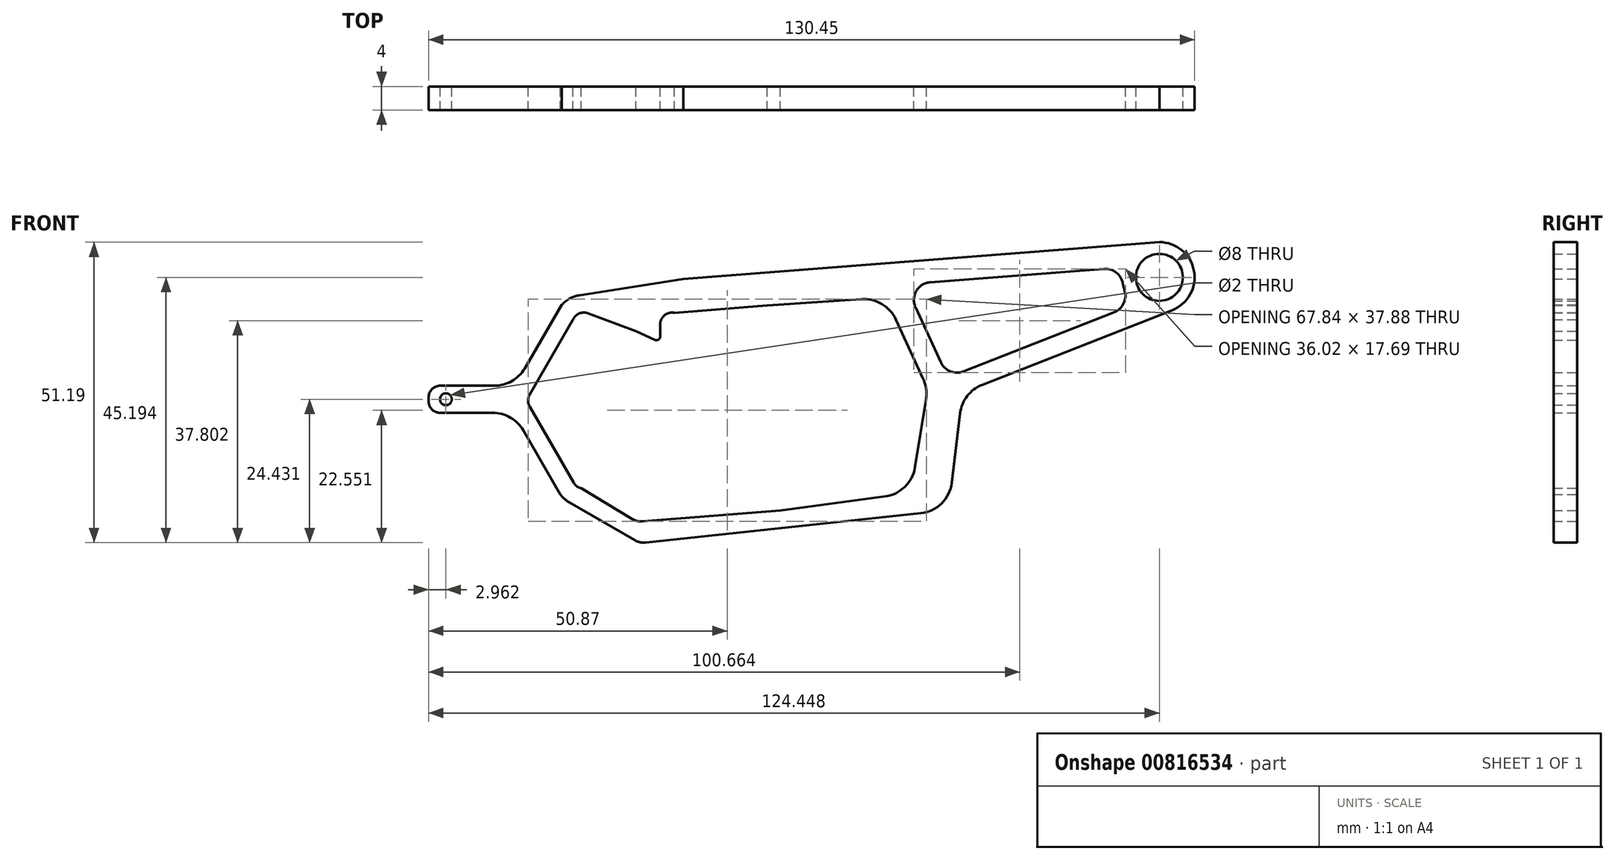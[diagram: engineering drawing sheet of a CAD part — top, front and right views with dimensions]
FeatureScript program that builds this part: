
annotation { "Feature Type Name" : "Feature", "Feature Type Description" : "" }
export const myFeature = defineFeature(function(context is Context, id is Id, definition is map)
    precondition{}
    {
        {
            assignVariable(context, id + "F0", {"name" : "GT_material", "anyValue" : 4});
        }
        {
            var Q0;
            Q0=qCreatedBy(makeId("Front.planeOp"),FACE);
            var sketch = newSketch(context, id + "F1", { "sketchPlane" : qUnion([Q0])});
            skCircle(sketch, "E0", {"center": v(51.48, 2.1) * mm, "radius": 4 * mm});
            skArc(sketch, "E1", {"start": v(57.48, 2.1) * mm, "mid": v(55.72, 6.35) * mm, "end": v(51.48, 8.1) * mm});
            skArc(sketch, "E2", {"start": v(53.67, -3.48) * mm, "mid": v(57.37, 3.22) * mm, "end": v(51.48, 8.1) * mm});
            skArc(sketch, "E3", {"start": v(-31.12, -3.94) * mm, "mid": v(-32.79, -4.35) * mm, "end": v(-33.52, -5.9) * mm});
            skLineSegment(sketch, "E4", {"start": v(-33.52, -5.89) * mm, "end": v(-33.52, -7.96) * mm});
            skLineSegment(sketch, "E5", {"start": v(-15.39, -2.7) * mm, "end": v(-31.12, -3.94) * mm});
            skLineSegment(sketch, "E6", {"start": v(-37.63, -7.07) * mm, "end": v(-34.47, -8.56) * mm});
            skPoint(sketch, "E7.visualSharp", {"position": v(-42.03, -5) * mm});
            skLineSegment(sketch, "E8", {"start": v(51.48, 8.1) * mm, "end": v(-29.58, 1.82) * mm});
            skLineSegment(sketch, "E9", {"start": v(17.55, -21.08) * mm, "end": v(16.16, -32.82) * mm});
            skLineSegment(sketch, "E10", {"start": v(-35.97, -43.08) * mm, "end": v(10.84, -38.08) * mm});
            skPoint(sketch, "E11.visualSharp", {"position": v(-40.07, -5.92) * mm});
            skPoint(sketch, "E12.visualSharp", {"position": v(10.59, -28.87) * mm});
            skArc(sketch, "E13", {"start": v(-45.83, -4.02) * mm, "mid": v(-47.3, -4.05) * mm, "end": v(-48.35, -5.08) * mm});
            skArc(sketch, "E14", {"start": v(-47.3, -0.96) * mm, "mid": v(-48.92, -1.5) * mm, "end": v(-50.26, -2.57) * mm});
            skLineSegment(sketch, "E15", {"start": v(-29.58, 1.82) * mm, "end": v(-47.3, -0.96) * mm});
            skLineSegment(sketch, "E16", {"start": v(-37.93, -6.96) * mm, "end": v(-45.83, -4.02) * mm});
            skLineSegment(sketch, "E17", {"start": v(-37.93, -6.96) * mm, "end": v(-37.63, -7.07) * mm});
            skArc(sketch, "E18", {"start": v(-55.75, -17.89) * mm, "mid": v(-56.02, -18.89) * mm, "end": v(-55.75, -19.89) * mm});
            skArc(sketch, "E19", {"start": v(-48.25, -32.88) * mm, "mid": v(-47.72, -33.48) * mm, "end": v(-46.98, -33.82) * mm});
            skArc(sketch, "E20", {"start": v(-58.56, -20.98) * mm, "mid": v(-58.35, -21.4) * mm, "end": v(-58.1, -21.78) * mm});
            skLineSegment(sketch, "E21", {"start": v(-50.26, -2.57) * mm, "end": v(-56.6, -13.4) * mm});
            skLineSegment(sketch, "E22", {"start": v(-56.83, -23.98) * mm, "end": v(-50.51, -34.89) * mm});
            skLineSegment(sketch, "E23", {"start": v(-49.02, -36.2) * mm, "end": v(-37.79, -42.7) * mm});
            skLineSegment(sketch, "E24", {"start": v(-48.35, -5.08) * mm, "end": v(-55.75, -17.89) * mm});
            skLineSegment(sketch, "E25", {"start": v(-55.75, -19.89) * mm, "end": v(-48.25, -32.88) * mm});
            skLineSegment(sketch, "E26", {"start": v(-46.98, -33.82) * mm, "end": v(-38.28, -39.05) * mm});
            skArc(sketch, "E27.trimOffspring", {"start": v(-51.12, -33.84) * mm, "mid": v(-50.26, -35.2) * mm, "end": v(-49.02, -36.2) * mm});
            skLineSegment(sketch, "E28.trimOffspring", {"start": v(-43.5, -35.86) * mm, "end": v(-43.48, -35.93) * mm});
            skPoint(sketch, "E29.visualSharp", {"position": v(-36.94, -43.18) * mm});
            skArc(sketch, "E29.filletArc", {"start": v(-37.79, -42.7) * mm, "mid": v(-36.91, -43.03) * mm, "end": v(-35.97, -43.08) * mm});
            skPoint(sketch, "E30.visualSharp", {"position": v(-37.46, -39.55) * mm});
            skArc(sketch, "E30.filletArc", {"start": v(-38.28, -39.05) * mm, "mid": v(-37.42, -39.4) * mm, "end": v(-36.5, -39.47) * mm});
            skLineSegment(sketch, "E31", {"start": v(-36.5, -39.47) * mm, "end": v(-13.1, -37.63) * mm});
            skPoint(sketch, "E32.visualSharp", {"position": v(-13.83, -2.57) * mm});
            skArc(sketch, "E32.filletArc", {"start": v(-15.32, -2.7) * mm, "mid": v(-15.35, -2.7) * mm, "end": v(-15.39, -2.7) * mm});
            skPoint(sketch, "E33.visualSharp", {"position": v(-11.61, -37.5) * mm});
            skPoint(sketch, "E34.visualSharp", {"position": v(-33.52, -9) * mm});
            skArc(sketch, "E34.filletArc", {"start": v(-34.47, -8.56) * mm, "mid": v(-33.83, -8.52) * mm, "end": v(-33.52, -7.96) * mm});
            skLineSegment(sketch, "E35", {"start": v(53.67, -3.48) * mm, "end": v(21.32, -16.2) * mm});
            skPoint(sketch, "E36.visualSharp", {"position": v(17.97, -17.51) * mm});
            skArc(sketch, "E36.filletArc", {"start": v(18.34, -17.37) * mm, "mid": v(18.06, -17.58) * mm, "end": v(17.93, -17.9) * mm});
            skArc(sketch, "E37.filletArc", {"start": v(21.32, -16.2) * mm, "mid": v(18.76, -18.12) * mm, "end": v(17.55, -21.08) * mm});
            skArc(sketch, "E38.filletArc", {"start": v(10.84, -38.08) * mm, "mid": v(14.42, -36.39) * mm, "end": v(16.16, -32.82) * mm});
            skLineSegment(sketch, "E39", {"start": v(-61.77, -16.36) * mm, "end": v(-70.96, -16.36) * mm});
            skLineSegment(sketch, "E40", {"start": v(-62.02, -20.98) * mm, "end": v(-70.97, -20.98) * mm});
            skLineSegment(sketch, "E41", {"start": v(-72.97, -18.95) * mm, "end": v(-72.96, -18.33) * mm});
            skPoint(sketch, "E42.visualSharp", {"position": v(-72.93, -16.36) * mm});
            skArc(sketch, "E42.filletArc", {"start": v(-72.2, -16.36) * mm, "mid": v(-72.72, -16.57) * mm, "end": v(-72.94, -17.1) * mm});
            skArc(sketch, "E43.filletArc", {"start": v(-70.96, -16.36) * mm, "mid": v(-72.37, -16.93) * mm, "end": v(-72.96, -18.33) * mm});
            skPoint(sketch, "E44.visualSharp", {"position": v(-73, -20.98) * mm});
            skArc(sketch, "E44.filletArc", {"start": v(-72.97, -18.95) * mm, "mid": v(-72.4, -20.39) * mm, "end": v(-70.97, -20.98) * mm});
            skCircle(sketch, "E45", {"center": v(-70, -18.66) * mm, "radius": 1 * mm});
            skPoint(sketch, "E46.visualSharp", {"position": v(-58.34, -16.36) * mm});
            skArc(sketch, "E46.filletArc", {"start": v(-61.77, -16.36) * mm, "mid": v(-58.8, -15.56) * mm, "end": v(-56.6, -13.4) * mm});
            skPoint(sketch, "E47.visualSharp", {"position": v(-58.56, -20.98) * mm});
            skArc(sketch, "E47.filletArc", {"start": v(-56.83, -23.98) * mm, "mid": v(-59.02, -21.79) * mm, "end": v(-62.02, -20.98) * mm});
            skLineSegment(sketch, "E48", {"start": v(9.86, -30.24) * mm, "end": v(11.74, -18.66) * mm});
            skLineSegment(sketch, "E49", {"start": v(11.27, -15.2) * mm, "end": v(6.62, -5.08) * mm});
            skLineSegment(sketch, "E50", {"start": v(0.76, -1.6) * mm, "end": v(-15.39, -2.7) * mm});
            skLineSegment(sketch, "E51", {"start": v(-13.1, -37.63) * mm, "end": v(4.74, -35.23) * mm});
            skPoint(sketch, "E52.visualSharp", {"position": v(4.89, -1.32) * mm});
            skArc(sketch, "E52.filletArc", {"start": v(6.62, -5.08) * mm, "mid": v(4.23, -2.43) * mm, "end": v(0.76, -1.6) * mm});
            skPoint(sketch, "E53.visualSharp", {"position": v(12.04, -16.86) * mm});
            skArc(sketch, "E53.filletArc", {"start": v(11.74, -18.66) * mm, "mid": v(11.77, -16.9) * mm, "end": v(11.27, -15.2) * mm});
            skPoint(sketch, "E54.visualSharp", {"position": v(9.15, -34.63) * mm});
            skArc(sketch, "E54.filletArc", {"start": v(4.74, -35.23) * mm, "mid": v(8.13, -33.58) * mm, "end": v(9.86, -30.24) * mm});
            skLineSegment(sketch, "E55", {"start": v(12.45, 1.26) * mm, "end": v(42.06, 3.56) * mm});
            skLineSegment(sketch, "E56", {"start": v(43.8, -3.82) * mm, "end": v(18.1, -13.92) * mm});
            skLineSegment(sketch, "E57", {"start": v(9.95, -2.99) * mm, "end": v(14.28, -12.39) * mm});
            skArc(sketch, "E58", {"start": v(45.25, 1.06) * mm, "mid": v(45.37, 0.51) * mm, "end": v(45.53, -0.02) * mm});
            skPoint(sketch, "E59.trimOffspring.end.orphan", {"position": v(18.28, -21.08) * mm});
            skPoint(sketch, "E60.visualSharp", {"position": v(8.15, 0.93) * mm});
            skArc(sketch, "E60.filletArc", {"start": v(12.45, 1.26) * mm, "mid": v(10.1, -0.21) * mm, "end": v(9.95, -2.99) * mm});
            skArc(sketch, "E61.filletArc", {"start": v(14.28, -12.39) * mm, "mid": v(15.88, -13.92) * mm, "end": v(18.1, -13.92) * mm});
            skArc(sketch, "E62.filletArc", {"start": v(43.8, -3.82) * mm, "mid": v(45.44, -2.27) * mm, "end": v(45.53, -0.02) * mm});
            skPoint(sketch, "E63.visualSharp", {"position": v(45.4, 3.82) * mm});
            skArc(sketch, "E63.filletArc", {"start": v(45.25, 1.06) * mm, "mid": v(44.14, 2.93) * mm, "end": v(42.06, 3.56) * mm});
            skSolve(sketch);
        }
        {
            var Q0;
            Q0=makeQuery(id+"F1.imprint","IMPRINT",FACE,{"disambiguationData":[TD([[makeQuery(id+"F1.imprint","IMPRINT",EDGE,{"derivedFrom":sQuery(id+"F1.wireOp",EDGE,"RTn5JsXc-azhZ-ol2G-LdRP-DOtyIP9GYYN3.bottom")}),-1.0]])]});
            var Q1;
            Q1=makeQuery(id+"F1.imprint","IMPRINT",FACE,{"disambiguationData":[TD([[makeQuery(id+"F1.imprint","IMPRINT",EDGE,{"derivedFrom":sQuery(id+"F1.wireOp",EDGE,"RTn5JsXc-azhZ-ol2G-LdRP-DOtyIP9GYYN3.left")}),1.0]])]});
            var Q2;
            {var subQ1=sQuery(id+"F1.wireOp",EDGE,"PgztXJE2-PVRy-cRri-htyC-8m0Y3nriVnsr");Q2=makeQuery(id+"F1.imprint","IMPRINT",FACE,{"disambiguationData":[TD([[makeQuery(id+"F1.imprint","IMPRINT",EDGE,{"derivedFrom":subQ1}),-1.0]])]});}
            var Q3;
            {var subQ0=sQuery(id+"F1.wireOp",EDGE,"115rUm4N-62Mg-SJ79-h6ah-3ekWXI7qW8Td");var subQ1=sQuery(id+"F1.wireOp",EDGE,"bnKybieg-NE3y-JRIe-mZQs-mjBHfe9F5jXf");var subQ2=makeQuery(id+"F1.imprint","INTERSECT",VERTEX,{"derivedFrom":[subQ1,subQ0]});Q3=makeQuery(id+"F1.imprint","IMPRINT",FACE,{"disambiguationData":[TD([[makeQuery(id+"F1.imprint","IMPRINT",EDGE,{"disambiguationData":[TD([[subQ2,-1.0]])],"derivedFrom":subQ1}),-1.0]])]});}
            var Q4;
            {var subQ3=sQuery(id+"F1.wireOp",EDGE,"bnKybieg-NE3y-JRIe-mZQs-mjBHfe9F5jXf");var subQ8=makeQuery(id+"F1.imprint","INTERSECT",VERTEX,{"derivedFrom":[subQ3,sQuery(id+"F1.wireOp",EDGE,"E9")]});Q4=makeQuery(id+"F1.imprint","IMPRINT",FACE,{"disambiguationData":[TD([[makeQuery(id+"F1.imprint","IMPRINT",EDGE,{"disambiguationData":[TD([[subQ8,1.0]])],"derivedFrom":subQ3}),-1.0]])]});}
            var Q5;
            {var subQ0=sQuery(id+"F1.wireOp",EDGE,"eEcY8RJj-clpU-FYRi-BO0Q-ZfVEHIXVT2eB");Q5=makeQuery(id+"F1.imprint","IMPRINT",FACE,{"disambiguationData":[TD([[makeQuery(id+"F1.imprint","IMPRINT",EDGE,{"derivedFrom":subQ0}),-1.0]])]});}
            var Q6;
            {var subQ0=sQuery(id+"F1.wireOp",EDGE,"E7.filletArc");Q6=makeQuery(id+"F1.imprint","IMPRINT",FACE,{"disambiguationData":[TD([[makeQuery(id+"F1.imprint","IMPRINT",EDGE,{"derivedFrom":subQ0}),1.0]])]});}
            var Q7;
            {var subQ0=sQuery(id+"F1.wireOp",EDGE,"E14");var subQ1=sQuery(id+"F1.wireOp",EDGE,"831c20b8-15d7-416d-bcb6-c6adbd6739e1.filletArc");var subQ2=makeQuery(id+"F1.imprint","INTERSECT",VERTEX,{"disambiguationData":[OD(0.0)],"derivedFrom":[subQ1,subQ0]});Q7=makeQuery(id+"F1.imprint","IMPRINT",FACE,{"disambiguationData":[TD([[makeQuery(id+"F1.imprint","IMPRINT",EDGE,{"disambiguationData":[TD([[subQ2,-1.0]])],"derivedFrom":subQ1}),1.0]])]});}
            var Q8;
            Q8=makeQuery(id+"F1.imprint","IMPRINT",FACE,{"disambiguationData":[TD([[makeQuery(id+"F1.imprint","IMPRINT",EDGE,{"derivedFrom":sQuery(id+"F1.wireOp",EDGE,"E13")}),-1.0]])]});
            var Q9;
            {var subQ0=sQuery(id+"F1.wireOp",EDGE,"E15");var subQ1=sQuery(id+"F1.wireOp",EDGE,"831c20b8-15d7-416d-bcb6-c6adbd6739e1.filletArc");var subQ2=makeQuery(id+"F1.imprint","INTERSECT",VERTEX,{"derivedFrom":[subQ1,subQ0]});Q9=makeQuery(id+"F1.imprint","IMPRINT",FACE,{"disambiguationData":[TD([[makeQuery(id+"F1.imprint","IMPRINT",EDGE,{"disambiguationData":[TD([[subQ2,-1.0]])],"derivedFrom":subQ1}),-1.0]])]});}
            var Q10;
            Q10=makeQuery(id+"F1.imprint","IMPRINT",FACE,{"disambiguationData":[TD([[makeQuery(id+"F1.imprint","IMPRINT",EDGE,{"derivedFrom":sQuery(id+"F1.wireOp",EDGE,"5ZnewX4w-Cjp8-ZgR4-c3zr-6juP8UMwIgxI")}),1.0]])]});
            var Q11;
            {var subQ1=sQuery(id+"F1.wireOp",EDGE,"eEcY8RJj-clpU-FYRi-BO0Q-ZfVEHIXVT2eB");Q11=makeQuery(id+"F1.imprint","IMPRINT",FACE,{"disambiguationData":[TD([[makeQuery(id+"F1.imprint","IMPRINT",EDGE,{"derivedFrom":subQ1}),1.0]])]});}
            extrude(context, id + "F2", {"entities" : qUnion([Q0, Q1, Q2, Q3, Q4, Q5, Q6, Q7, Q8, Q9, Q10, Q11]), "depth" : (getVariable(context, 'GT_material')) * mm, "offsetDistance" : 25 * mm});
        }
    });
